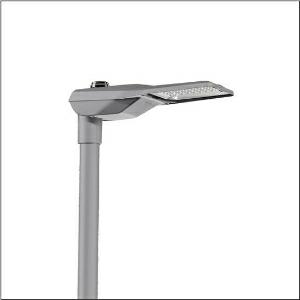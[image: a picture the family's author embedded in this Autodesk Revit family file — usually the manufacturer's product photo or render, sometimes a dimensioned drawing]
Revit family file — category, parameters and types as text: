
# Revit family: streetlight_sl_21_mini___st1_5a_5xe6p37n08hb_7a86
name_source: partatom
category: Lighting Fixtures
units: mm (PartAtom-declared; Revit-internal decimal feet)

## family parameters
Cut with Voids When Loaded = No
Host = Face
Light Source = No
Part Type = Normal
Room Calculation Point = No
Round Connector Dimension = Use Diameter
Shared = No

## types (1)
- --- (1 x LED, 8890 lm, 66 W, 3000K)
    Apparent Load = 66 VA
    CIE Flux Codes = 22 53 95 100 100
    Color Rendering = 70
    Color Temperature = 3000K
    Default Elevation = 1800 mm
    Description = Streetlight SL 21 mini, mast luminaire, primary light control with lens, of PMMA, primary optical cover: cover, of toughened safety glass, transparent, light distribution: ST1.5a, light emission: direct distribution, primary light characteristic: asymmetric, installation type: side-entry, LED, 3G 1.5mm², High Power LED, rated luminous flux: 8.890lm, luminous efficacy: 135lm/W, light colour: 730, colour temperature: 3000K, control gear: NEMA (7pin), control: overheat protection, pre-setting: linear dimming characteristic, constant luminous flux control, time-dependent luminous flux control, flexible luminous flux parameterisation, mains connection: 230..240V, AC, 50/60Hz, connection cable pre-assembled, cable length: 8,5m, wiring characteristics: H07RN-F, start of lifetime: 66W, end of service life: 69W, reduction: 30W, luminaire housing, of diecast aluminium (EN AC-44300), powder-coated, SITECO metallic grey (DB 702S), corrosivity category C5 high according to DIN EN ISO 12944, multi-level sealing system, sealing non-destructively replaceable, inclination adjustable: 0°, 5°, 10°, 15°, length: 628mm, width: 235mm, height: 110mm, spigot size: 42mm (side-entry), mounting height: 4..8m, protection rating (complete): IP66, insulation class (complete): insulation class I (protective earthing), certification: CE, ENEC, ENEC+, VDE, impact resistance: IK10, permissible operating ambient temperature for outdoor applications: -40..+50°C, standard-compliant lighting for roads and squares, packaging unit: 1 piece

Light Distribution: ST1.5a
    Height = 110 mm
    Lamp = 1 x LED
    Lamp Light Flux = 8890 lm
    Lamp Power = 66 W
    Lamp count = 1
    Length = 625 mm
    Luminous efficacy = 135 lm/W
    Manufacturer = Siteco
    ModVariant = No
    Model = 5XE6P37N08HB
    Number of Poles = 1
    OnlyDefault = Yes
    Power Factor = 1
    Product Name = Streetlight SL 21 mini | ST1.5a
    Product group = mast luminaire | pylon top
    ProductGroupID = 6100
    Protection Class = Protection class I
    Protection Degree = IP 66
    RLX_Detail_Level = 1
    RLX_Emergency_Light_Flux = 0 lm
    RLX_Emergency_Type = 0
    RLX_Emergency_Type_DB = No
    RlxData = <blob elided: 29657 chars, md5=7f1e070d>
    Socket = socket
    Standby Power = 0 W
    System Light Flux = 8890 lm
    System Power = 66 W
    Type Comments = factory setting: luminous flux: 100 % | dim-lin: 254 | 670 mA
    Type Image = l_1294379.jpg
    URL = http://relux.com
    VarID = @adj_133113
    Voltage = 0 V
    Weight = 0.00 kg
    Width = 234 mm

## geometry (parser evidence)
native form markers: Blend x4, Sweep x9
no freeform markers — native parametric forms only
